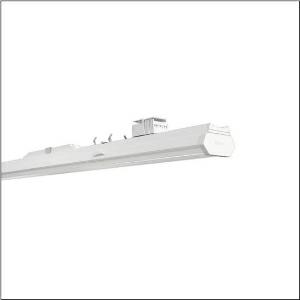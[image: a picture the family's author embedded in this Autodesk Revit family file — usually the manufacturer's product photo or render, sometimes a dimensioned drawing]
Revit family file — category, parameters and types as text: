
# Revit family: licross_r__21_protected_mo_52tp11cn49xg_f153
name_source: partatom
category: Lighting Fixtures
units: mm (PartAtom-declared; Revit-internal decimal feet)

## family parameters
Cut with Voids When Loaded = No
Host = Face
Light Source = No
Part Type = Normal
Room Calculation Point = No
Round Connector Dimension = Use Diameter
Shared = No

## types (1)
- --- (1 x LED, 9070 lm, 50.4 W, 4000K)
    Apparent Load = 50 VA
    CIE Flux Codes = 83 94 98 100 100
    Color Rendering = 80
    Color Temperature = 4000K
    Default Elevation = 1800 mm
    Description = Licross® 21 Protected MO, luminaire insert, of sheet steel, galvanised, coil coated, white, length: 1.500mm, width: 90mm, height: 103mm, LED rated luminous flux: 9.080lm, light colour: 840, control gear: ON/OFF Multilumen, CLOi, control gear: ECG Multilumen, with plug, 3-pole, with phase selection, mains connection: 220..240V, AC, 50/60Hz, start of lifetime: 50W, end of service life: 61W, halogen-free wiring, primary light control with lens, of plastic, primary optical cover: cover, of PMMA, light emission: direct distribution, primary light characteristic: symmetric, protection rating (complete): IP64, insulation class (complete): insulation class I (protective earthing), certification: CE, ENEC, VDE, UKCA, protection symbol: D if used in an environment with conductive dust loads with corresponding accessories, impact resistance: IK06, permissible ambient temperature for indoor applications: -35..+45°C, corresponds to IFS (International Featured Standards) requirements for safety and quality in the food industry, reducing of maximum allowable ambient temperature of 5°C with ceiling mounting, LABS conformity tested according to VDMA 24364:2018-05, packaging unit: 1 piece
    Height = 92 mm
    Lamp = 1 x LED
    Lamp Light Flux = 9070 lm
    Lamp Power = 50.4 W
    Lamp count = 1
    Length = 1500 mm
    Luminous efficacy = 180 lm/W
    Manufacturer = Siteco
    ModVariant = No
    Model = 52TP11CN49XG
    Mounting Place = Ceiling
    Mounting Type = Pendant
    Number of Poles = 1
    OnlyDefault = Yes
    Power Factor = 1
    Product Name = Licross® 21 Protected MO
    Product group = luminaire insert
    ProductGroupID = 902
    Protection Class = Protection class I
    Protection Degree = IP 64
    RLX_Detail_Level = 1
    RLX_Emergency_Light_Flux = 0 lm
    RLX_Emergency_Type = 0
    RLX_Emergency_Type_DB = No
    RlxData = <blob elided: 21841 chars, md5=a27218a0>
    Socket = socket
    Standby Power = 0 W
    System Light Flux = 9070 lm
    System Power = 50 W
    Type Comments = factory setting: luminous flux: 100 % | (A | C | E) | 117 mA
    Type Image = l_1256148.jpg
    URL = http://relux.com
    VarID = @adj_110862
    Voltage = 0 V
    Weight = 0.00 kg
    Width = 88 mm

## geometry (parser evidence)
native form markers: Blend x4, Sweep x12
no freeform markers — native parametric forms only
